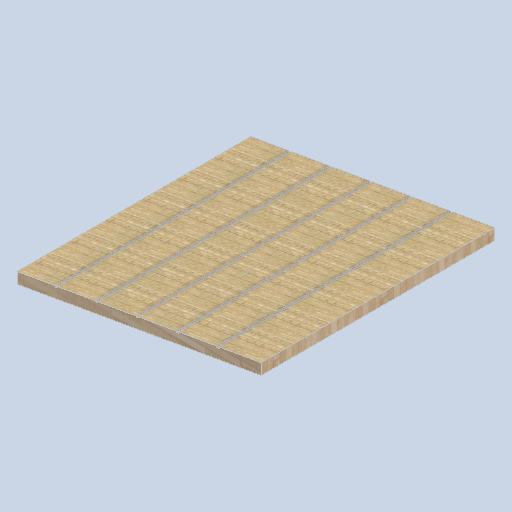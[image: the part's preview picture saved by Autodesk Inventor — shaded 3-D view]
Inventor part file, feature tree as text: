
AUTODESK INVENTOR PART (.ipt)
format: ipt  version: 2024.2 (Build 282272000, 272)  size: 251,392 bytes
history: native  units: in
note: dims shown in document units (in); Inventor stores cm internally (conversion verified against a paired STEP export)
features: sketch x4, other x3, plane x3
ambient origin geometry x8: Origin, YZ Plane, XZ Plane, XY Plane, X Axis, Y Axis, Z Axis, Center Point
bodies: Solid1 (feature_tree)
feature tree (10):
  other  "eave_panel_side_.ipt"
  other  "Solid1::eave_panel_side_.ipt"
  other  "TaggingFeature1"
  sketch  "Sketch1"  dims[d0=0.3937in]
  sketch  "Sketch2"
  sketch  "Sketch3"
  sketch  "Sketch4"
  plane  "Work Plane1"
  plane  "Work Plane2"
  plane  "Work Plane3"
